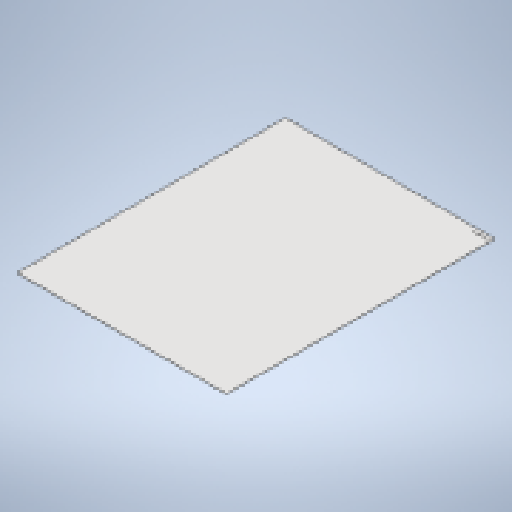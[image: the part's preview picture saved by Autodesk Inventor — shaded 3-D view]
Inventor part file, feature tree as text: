
AUTODESK INVENTOR PART (.ipt)
format: ipt  version: 2025 (Build 290162010, 162A)  size: 220,672 bytes
history: native  units: mm
features: other x3, sketch x2, sheet_metal_op x1
ambient origin geometry x8: Origin, YZ Plane, XZ Plane, XY Plane, X Axis, Y Axis, Z Axis, Center Point
bodies: Body1 (feature_tree)
feature tree (6):
  sheet_metal_op  "Face3"
  other  "Mark1"
  sketch  "Sketch6"  dims[d40=1479.0mm]
  other  "Plate5"
  sketch  "Sketch7"  dims[d41=1895.0mm d42=3.0mm d43=200.0mm d44=15.0mm d45=25.0mm d46=25.0mm]
  other  "Definition1"
